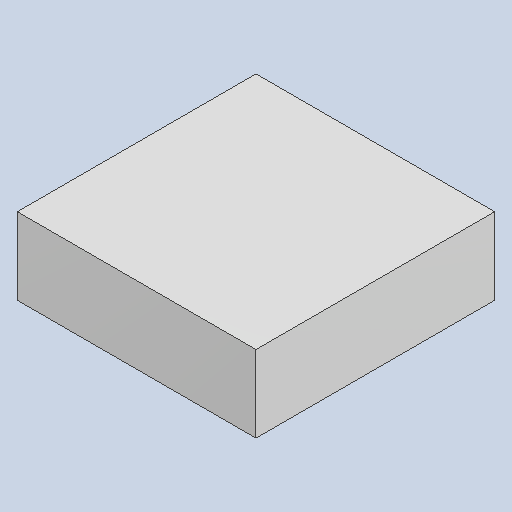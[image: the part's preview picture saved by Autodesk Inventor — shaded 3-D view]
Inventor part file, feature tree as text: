
AUTODESK INVENTOR PART (.ipt)
format: ipt  version: 2023.4 (Build 274418000, 418)  size: 79,872 bytes
history: native  units: mm
features: extrude x1
ambient origin geometry x8: Origin, YZ Plane, XZ Plane, XY Plane, X Axis, Y Axis, Z Axis, Center Point
bodies: Solid1 (feature_tree)
feature tree (1):
  extrude  "Extruded_5"  [1 undecoded]
note: 1 required parameter value undecoded (feature->parameter linkage not recoverable at this tier; creation-order binding heuristic only, values carry confidence <= 0.55)
